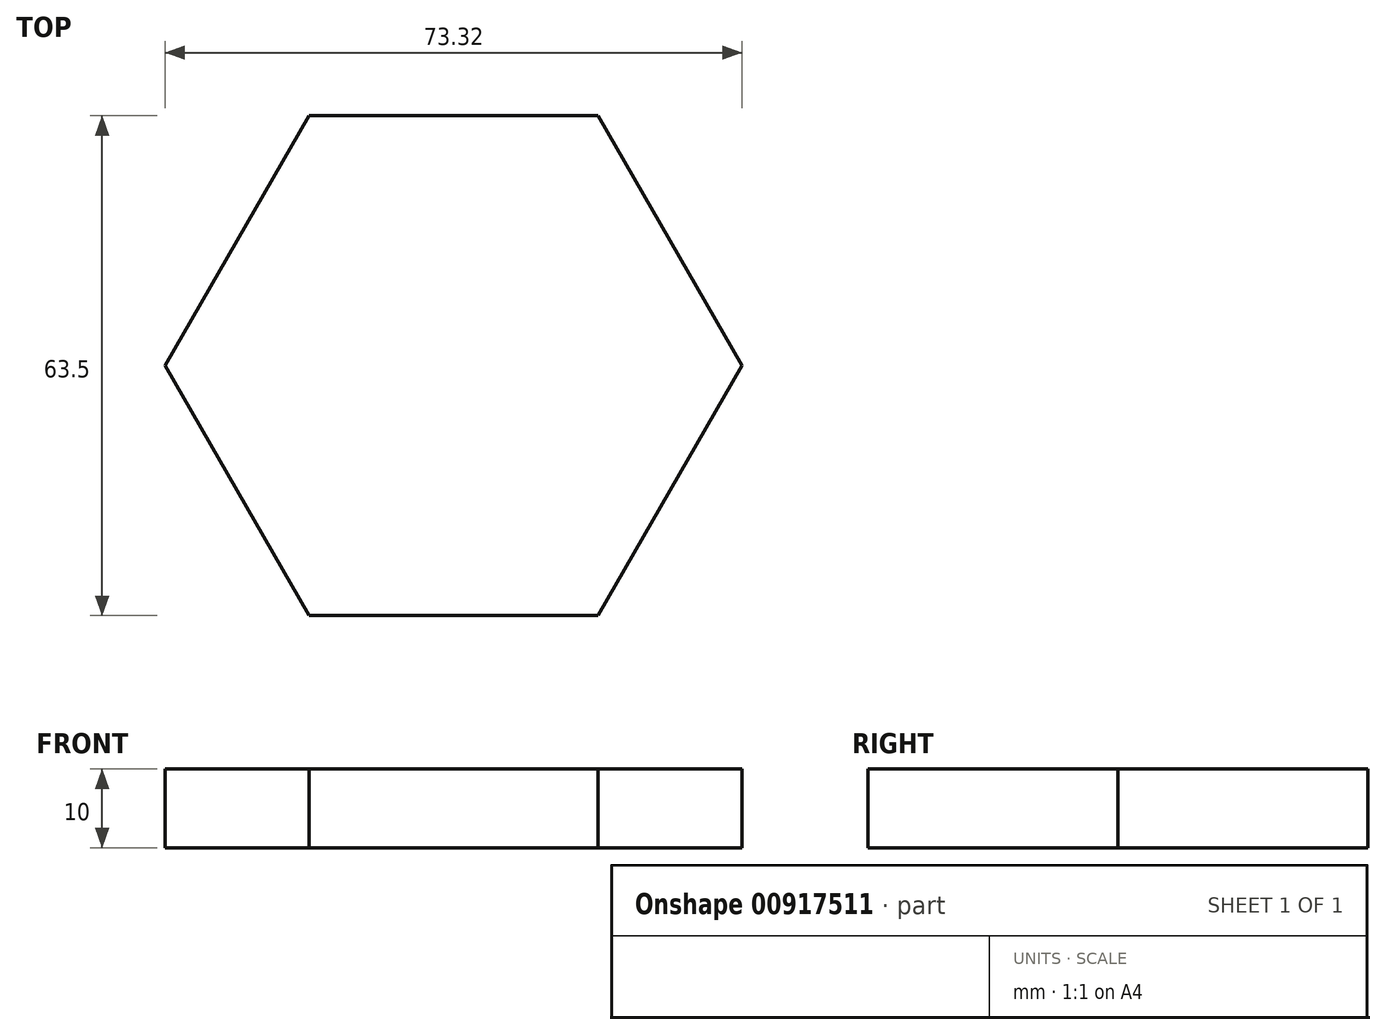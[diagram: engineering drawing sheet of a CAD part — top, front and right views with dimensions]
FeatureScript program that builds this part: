
annotation { "Feature Type Name" : "Feature", "Feature Type Description" : "" }
export const myFeature = defineFeature(function(context is Context, id is Id, definition is map)
    precondition{}
    {
        {
            var Q0;
            Q0=qCreatedBy(makeId("Top.planeOp"),FACE);
            var sketch = newSketch(context, id + "F0", { "sketchPlane" : qUnion([Q0])});
            skCircle(sketch, "E0.cCircle", {"center": v(0, 0) * mm, "radius": 31.75 * mm, "construction": true});
            skLineSegment(sketch, "E0.0", {"start": v(36.66, 0) * mm, "end": v(18.33, -31.75) * mm});
            skLineSegment(sketch, "E0.1", {"start": v(18.33, -31.75) * mm, "end": v(-18.33, -31.75) * mm});
            skLineSegment(sketch, "E0.2", {"start": v(-18.33, -31.75) * mm, "end": v(-36.66, 0) * mm});
            skLineSegment(sketch, "E0.3", {"start": v(-36.66, 0) * mm, "end": v(-18.33, 31.75) * mm});
            skLineSegment(sketch, "E0.4", {"start": v(-18.33, 31.75) * mm, "end": v(18.33, 31.75) * mm});
            skLineSegment(sketch, "E0.5", {"start": v(18.33, 31.75) * mm, "end": v(36.66, 0) * mm});
            skPoint(sketch, "E0.0.midPoint", {"position": v(27.5, -15.88) * mm});
            skSolve(sketch);
        }
        {
            var Q0;
            Q0 = qSketchRegion(id + "F0", true);
            extrude(context, id + "F1", {"entities" : qUnion([Q0]), "depth" : 10 * mm, "offsetDistance" : 25.4 * mm});
        }
    });
